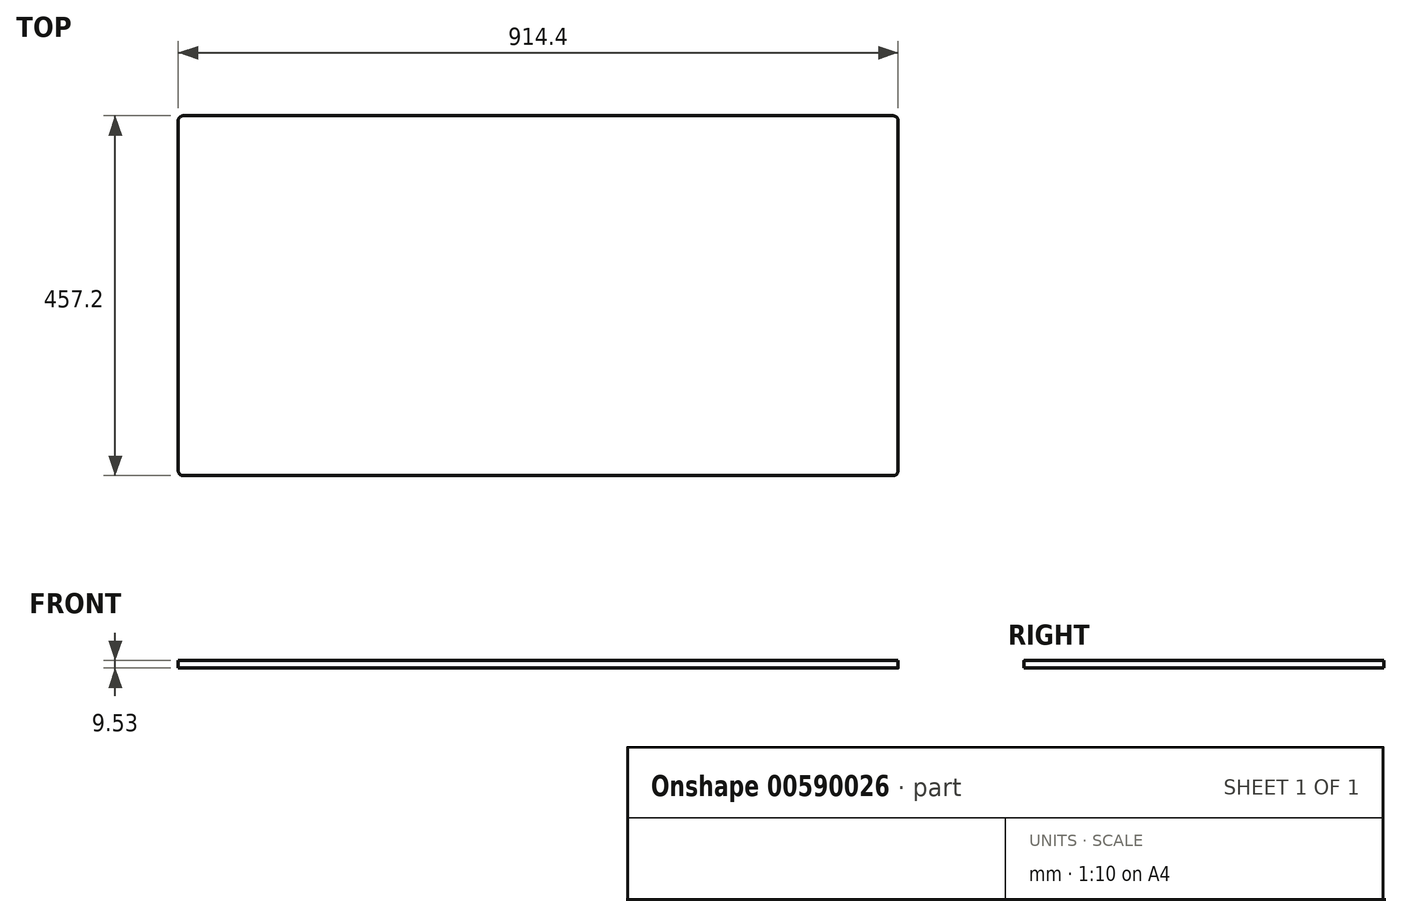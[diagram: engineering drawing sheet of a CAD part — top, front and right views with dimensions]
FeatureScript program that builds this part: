
annotation { "Feature Type Name" : "Feature", "Feature Type Description" : "" }
export const myFeature = defineFeature(function(context is Context, id is Id, definition is map)
    precondition{}
    {
        {
            var Q0;
            Q0=qCreatedBy(makeId("Top.planeOp"),FACE);
            var sketch = newSketch(context, id + "F0", { "sketchPlane" : qUnion([Q0])});
            skLineSegment(sketch, "E0", {"start": v(-403.5, 0) * mm, "end": v(510.9, 0) * mm});
            skLineSegment(sketch, "E1", {"start": v(-403.5, 0) * mm, "end": v(-403.5, 457.2) * mm});
            skLineSegment(sketch, "E2", {"start": v(-403.5, 457.2) * mm, "end": v(510.9, 457.2) * mm});
            skLineSegment(sketch, "E3", {"start": v(510.9, 457.2) * mm, "end": v(510.9, 0) * mm});
            skSolve(sketch);
        }
        {
            var Q0;
            Q0 = qSketchRegion(id + "F0", true);
            extrude(context, id + "F1", {"entities" : qUnion([Q0]), "oppositeDirection" : true, "depth" : 9.52 * mm, "offsetDistance" : 25.4 * mm});
        }
        {
            var Q0;
            Q0=makeQuery(id+"F1.opExtrude","SWEPT_EDGE",EDGE,{"disambiguationData":[OSD([sQuery(id+"F0.wireOp",EDGE,"E1"),sQuery(id+"F0.wireOp",EDGE,"E2")])]});
            var Q1;
            Q1=makeQuery(id+"F1.opExtrude","SWEPT_EDGE",EDGE,{"disambiguationData":[OSD([sQuery(id+"F0.wireOp",EDGE,"E0"),sQuery(id+"F0.wireOp",EDGE,"E1")])]});
            var Q2;
            Q2=makeQuery(id+"F1.opExtrude","SWEPT_EDGE",EDGE,{"disambiguationData":[OSD([sQuery(id+"F0.wireOp",EDGE,"E0"),sQuery(id+"F0.wireOp",EDGE,"E3")])]});
            var Q3;
            Q3=makeQuery(id+"F1.opExtrude","SWEPT_EDGE",EDGE,{"disambiguationData":[OSD([sQuery(id+"F0.wireOp",EDGE,"E2"),sQuery(id+"F0.wireOp",EDGE,"E3")])]});
            fillet(context, id + "F2", {"entities" : qUnion([Q0, Q1, Q2, Q3]), "radius" : 6.35 * mm, "tangentPropagation" : true, "allowEdgeOverflow" : false});
        }
    });
